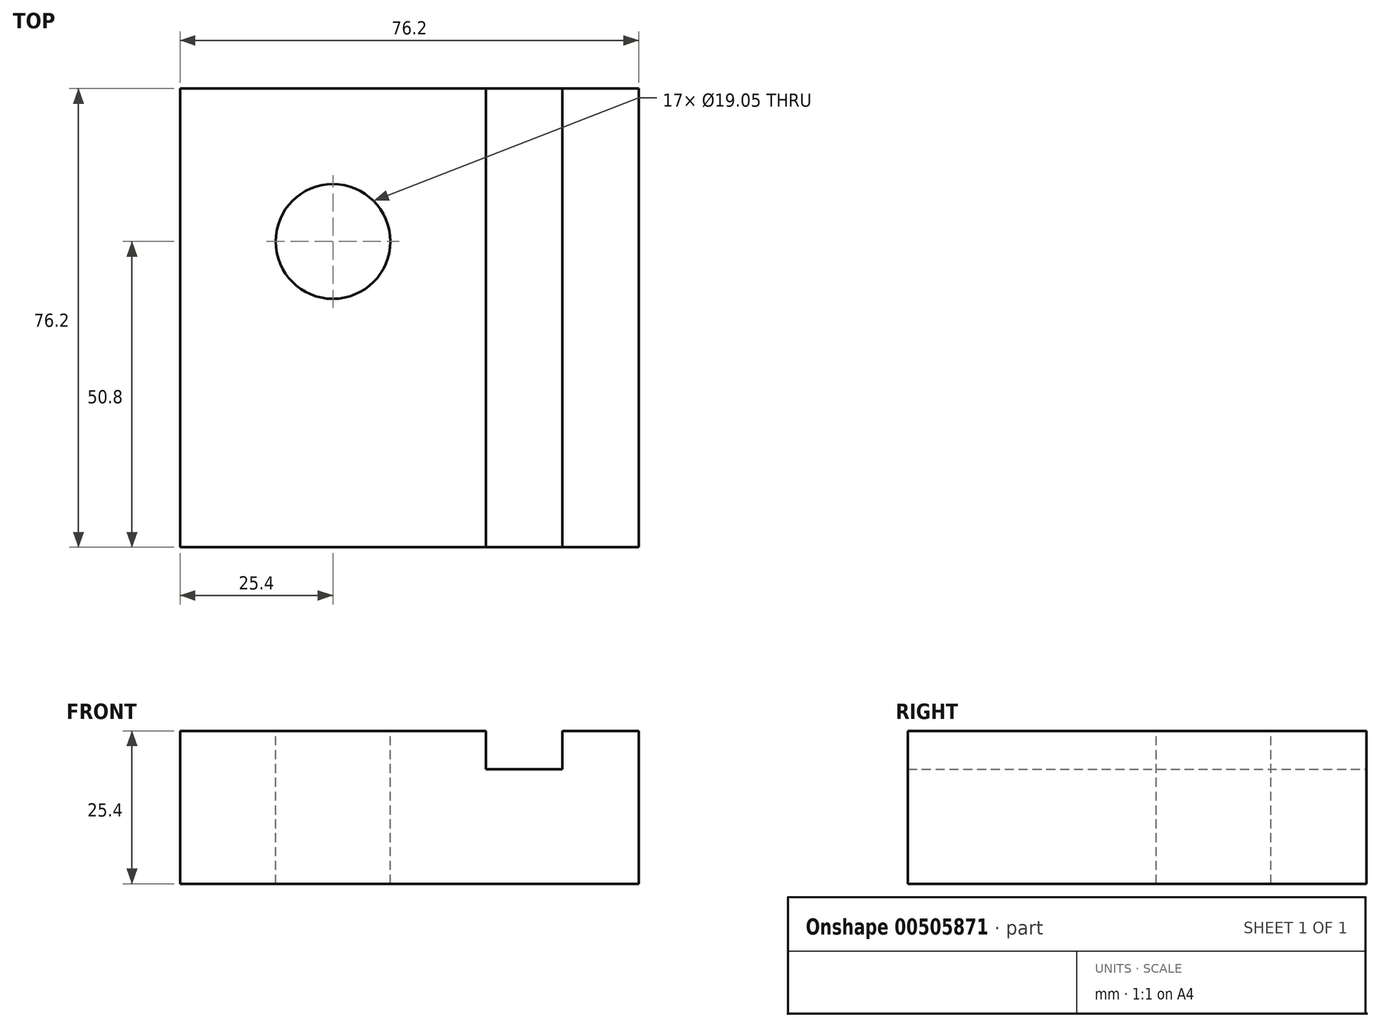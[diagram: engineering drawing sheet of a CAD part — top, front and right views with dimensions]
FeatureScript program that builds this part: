
annotation { "Feature Type Name" : "Feature", "Feature Type Description" : "" }
export const myFeature = defineFeature(function(context is Context, id is Id, definition is map)
    precondition{}
    {
        {
            var Q0;
            Q0=qCreatedBy(makeId("Front.planeOp"),FACE);
            var sketch = newSketch(context, id + "F0", { "sketchPlane" : qUnion([Q0])});
            skLineSegment(sketch, "E0.bottom", {"start": v(0, 0) * mm, "end": v(76.2, 0) * mm});
            skLineSegment(sketch, "E0.left", {"start": v(0, 0) * mm, "end": v(0, 25.4) * mm});
            skLineSegment(sketch, "E0.right", {"start": v(76.2, 0) * mm, "end": v(76.2, 25.4) * mm});
            skLineSegment(sketch, "E1", {"start": v(0, 25.4) * mm, "end": v(50.8, 25.4) * mm});
            skLineSegment(sketch, "E2", {"start": v(50.8, 25.4) * mm, "end": v(50.8, 19.05) * mm});
            skLineSegment(sketch, "E3", {"start": v(50.8, 19.05) * mm, "end": v(63.5, 19.05) * mm});
            skLineSegment(sketch, "E4", {"start": v(63.5, 19.05) * mm, "end": v(63.5, 25.4) * mm});
            skLineSegment(sketch, "E5", {"start": v(63.5, 25.4) * mm, "end": v(76.2, 25.4) * mm});
            skSolve(sketch);
        }
        {
            var Q0;
            Q0=makeQuery(id+"F0.imprint","IMPRINT",FACE,{"disambiguationData":[TD([[makeQuery(id+"F0.imprint","IMPRINT",EDGE,{"derivedFrom":sQuery(id+"F0.wireOp",EDGE,"E0.bottom")}),1.0]])]});
            extrude(context, id + "F1", {"entities" : qUnion([Q0]), "depth" : 76.2 * mm});
        }
        {
            var Q0;
            Q0=makeQuery(id+"F1.opExtrude","SWEPT_FACE",FACE,{"disambiguationData":[OSD([sQuery(id+"F0.wireOp",EDGE,"E1")])]});
            var sketch = newSketch(context, id + "F2", { "sketchPlane" : qUnion([Q0])});
            skLineSegment(sketch, "E6", {"start": v(0, 0) * mm, "end": v(25.4, 0) * mm, "construction": true});
            skLineSegment(sketch, "E7", {"start": v(25.4, 0) * mm, "end": v(25.4, -25.4) * mm, "construction": true});
            skCircle(sketch, "E8", {"center": v(25.4, -25.4) * mm, "radius": 9.53 * mm});
            skSolve(sketch);
        }
        {
            var Q0;
            Q0=makeQuery(id+"F2.imprint","IMPRINT",FACE,{"disambiguationData":[TD([[makeQuery(id+"F2.imprint","IMPRINT",EDGE,{"derivedFrom":sQuery(id+"F2.wireOp",EDGE,"E8")}),1.0]])]});
            var Q1;
            Q1=sQuery(id+"F2.wireOp",EDGE,"E8");
            extrude(context, id + "F3", {"entities" : qUnion([Q0]), "operationType" : NewBodyOperationType.REMOVE, "surfaceEntities" : qUnion([Q1]), "endBound" : BoundingType.THROUGH_ALL, "oppositeDirection" : true, "depth" : 76.2 * mm});
        }
    });
